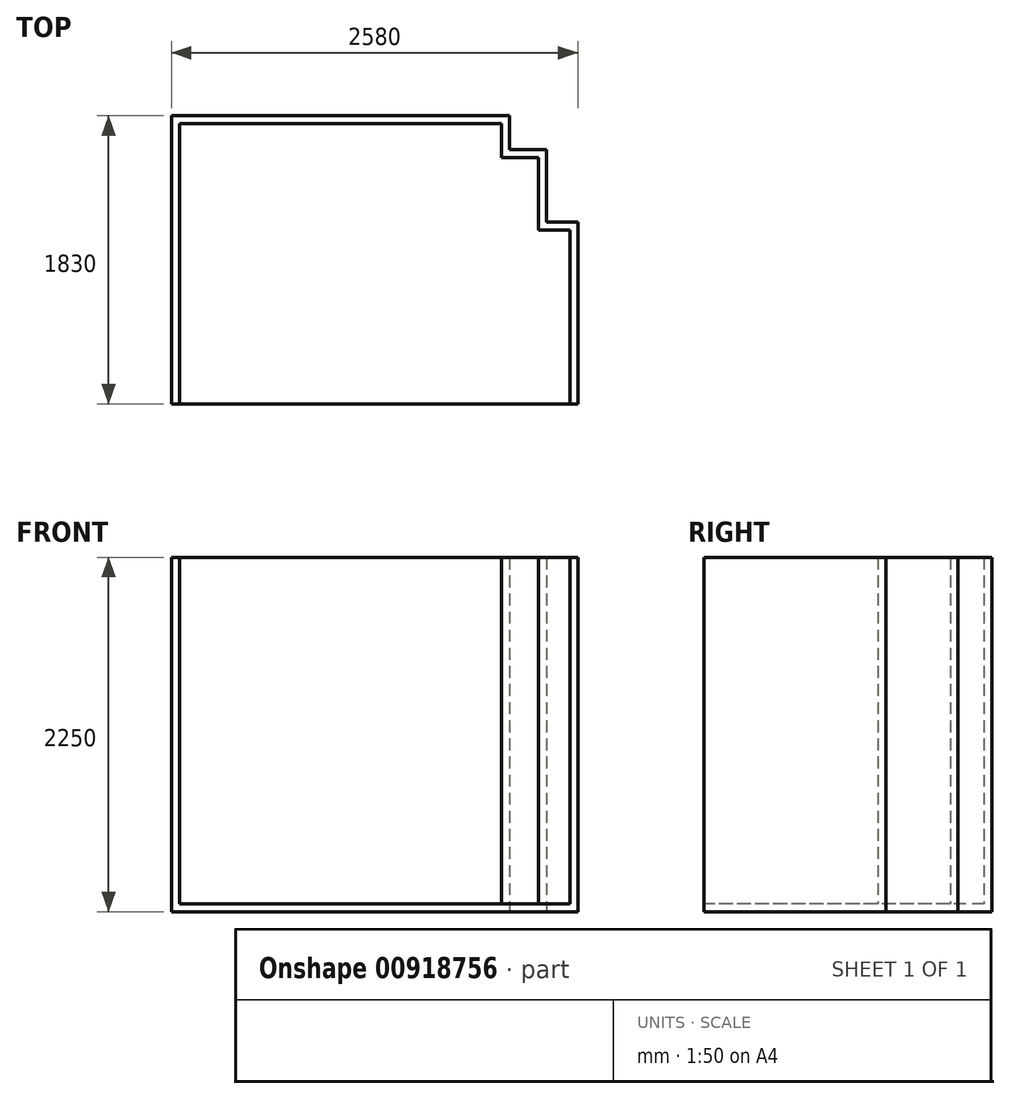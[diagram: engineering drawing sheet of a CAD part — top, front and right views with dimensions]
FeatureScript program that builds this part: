
annotation { "Feature Type Name" : "Feature", "Feature Type Description" : "" }
export const myFeature = defineFeature(function(context is Context, id is Id, definition is map)
    precondition{}
    {
        {
            var Q0;
            Q0=qCreatedBy(makeId("Top.planeOp"),FACE);
            var sketch = newSketch(context, id + "F0", { "sketchPlane" : qUnion([Q0])});
            skLineSegment(sketch, "E0", {"start": v(0, 0) * mm, "end": v(0, -1780) * mm});
            skLineSegment(sketch, "E1", {"start": v(0, 0) * mm, "end": v(2045, 0) * mm});
            skLineSegment(sketch, "E2", {"start": v(2045, 0) * mm, "end": v(2045, -215) * mm});
            skLineSegment(sketch, "E3", {"start": v(2045, -215) * mm, "end": v(2280, -215) * mm});
            skLineSegment(sketch, "E4", {"start": v(2280, -215) * mm, "end": v(2280, -675) * mm});
            skLineSegment(sketch, "E5", {"start": v(2280, -675) * mm, "end": v(2480, -675) * mm});
            skLineSegment(sketch, "E6", {"start": v(2480, -675) * mm, "end": v(2480, -1780) * mm});
            skLineSegment(sketch, "E7", {"start": v(0, -1780) * mm, "end": v(2480, -1780) * mm, "construction": true});
            skLineSegment(sketch, "E8.0", {"start": v(2530, -625) * mm, "end": v(2530, -1780) * mm});
            skLineSegment(sketch, "E8.1", {"start": v(2330, -625) * mm, "end": v(2530, -625) * mm});
            skLineSegment(sketch, "E8.2", {"start": v(2330, -165) * mm, "end": v(2330, -625) * mm});
            skLineSegment(sketch, "E8.3", {"start": v(-50, 50) * mm, "end": v(-50, -1780) * mm});
            skLineSegment(sketch, "E8.4", {"start": v(-50, 50) * mm, "end": v(2095, 50) * mm});
            skLineSegment(sketch, "E8.5", {"start": v(2095, 50) * mm, "end": v(2095, -165) * mm});
            skLineSegment(sketch, "E8.6", {"start": v(2095, -165) * mm, "end": v(2330, -165) * mm});
            skLineSegment(sketch, "E9", {"start": v(2480, -1780) * mm, "end": v(2530, -1780) * mm});
            skLineSegment(sketch, "E10", {"start": v(-50, -1780) * mm, "end": v(0, -1780) * mm});
            skSolve(sketch);
        }
        {
            var Q0;
            Q0 = qSketchRegion(id + "F0", true);
            extrude(context, id + "F1", {"entities" : qUnion([Q0]), "depth" : 2200 * mm, "offsetDistance" : 25 * mm});
        }
        {
            var Q0;
            Q0=makeQuery(id+"F1.opExtrude","CAP_FACE",FACE,{"disambiguationData":[OSD([sQuery(id+"F0.wireOp",EDGE,"E0"),sQuery(id+"F0.wireOp",EDGE,"E1"),sQuery(id+"F0.wireOp",EDGE,"E2"),sQuery(id+"F0.wireOp",EDGE,"E3"),sQuery(id+"F0.wireOp",EDGE,"E4"),sQuery(id+"F0.wireOp",EDGE,"E5"),sQuery(id+"F0.wireOp",EDGE,"E6"),sQuery(id+"F0.wireOp",EDGE,"E8.0"),sQuery(id+"F0.wireOp",EDGE,"E8.1"),sQuery(id+"F0.wireOp",EDGE,"E8.2"),sQuery(id+"F0.wireOp",EDGE,"E8.3"),sQuery(id+"F0.wireOp",EDGE,"E8.4"),sQuery(id+"F0.wireOp",EDGE,"E8.5"),sQuery(id+"F0.wireOp",EDGE,"E8.6"),sQuery(id+"F0.wireOp",EDGE,"E9"),sQuery(id+"F0.wireOp",EDGE,"E10")])],"isStart":true});
            var sketch = newSketch(context, id + "F2", { "sketchPlane" : qUnion([Q0])});
            skLineSegment(sketch, "E11.0", {"start": v(-50, -50) * mm, "end": v(-50, 1780) * mm});
            skLineSegment(sketch, "E11.1", {"start": v(-50, -50) * mm, "end": v(2095, -50) * mm});
            skLineSegment(sketch, "E11.2", {"start": v(2095, 165) * mm, "end": v(2330, 165) * mm});
            skLineSegment(sketch, "E11.3", {"start": v(2095, -50) * mm, "end": v(2095, 165) * mm});
            skLineSegment(sketch, "E11.4", {"start": v(2330, 165) * mm, "end": v(2330, 625) * mm});
            skLineSegment(sketch, "E11.5", {"start": v(2330, 625) * mm, "end": v(2530, 625) * mm});
            skLineSegment(sketch, "E11.6", {"start": v(2530, 625) * mm, "end": v(2530, 1780) * mm});
            skLineSegment(sketch, "E12", {"start": v(-50, 1780) * mm, "end": v(2530, 1780) * mm});
            skSolve(sketch);
        }
        {
            var Q0;
            Q0 = qSketchRegion(id + "F2", true);
            extrude(context, id + "F3", {"entities" : qUnion([Q0]), "operationType" : NewBodyOperationType.ADD, "depth" : 50 * mm, "offsetDistance" : 25 * mm});
        }
    });
